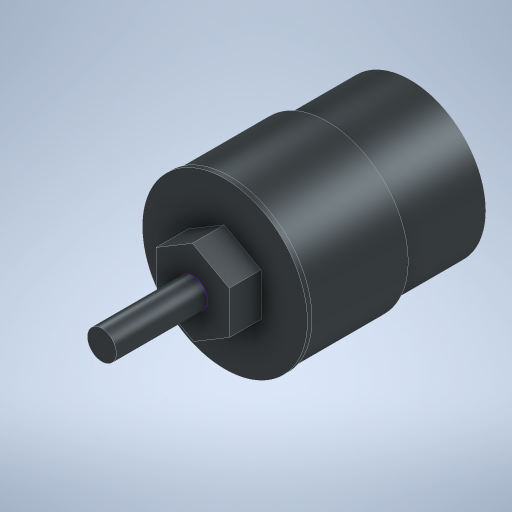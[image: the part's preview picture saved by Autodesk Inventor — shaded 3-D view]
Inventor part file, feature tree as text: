
AUTODESK INVENTOR PART (.ipt)
format: ipt  version: 2023 (Build 270158000, 158)  size: 278,528 bytes
history: native  units: in
note: dims shown in document units (in); Inventor stores cm internally (conversion verified against a paired STEP export)
features: sketch x10, extrude x7
ambient origin geometry x8: Origin, YZ Plane, XZ Plane, XY Plane, X Axis, Y Axis, Z Axis, Center Point
bodies: Solid1 (feature_tree)
feature tree (17):
  extrude  "Extrusion1"  Depth=0.7165in TaperAngle=0.0deg
  extrude  "Extrusion2"  Depth=0.3937in TaperAngle=0.0deg
  extrude  "Extrusion5"  Depth=0.2756in TaperAngle=0.0deg
  extrude  "Extrusion3"  [1 undecoded]
  sketch  "Sketch4"  dims[d12=0.7874in d13=0.0in]
  extrude  "Extrusion4"  [1 undecoded]
  sketch  "Sketch6"
  sketch  "Sketch7"
  sketch  "Sketch8"
  extrude  "Extrusion6"  [1 undecoded]
  sketch  "Sketch9"
  extrude  "Extrusion7"  [1 undecoded]
  sketch  "3D Sketch1"
  sketch  "Sketch1"  dims[d0=0.8445in d1=0.0in d2=0.7165in d3=0.0in]
  sketch  "Sketch2"  dims[d4=0.3937in d5=0.0in d6=0.3937in d7=0.0in]
  sketch  "Sketch3"  dims[d8=0.0394in d9=0.0in d10=0.2756in d11=0.0in]
  sketch  "Sketch5"
note: 4 required parameter values undecoded (feature->parameter linkage not recoverable at this tier; creation-order binding heuristic only, values carry confidence <= 0.55)
